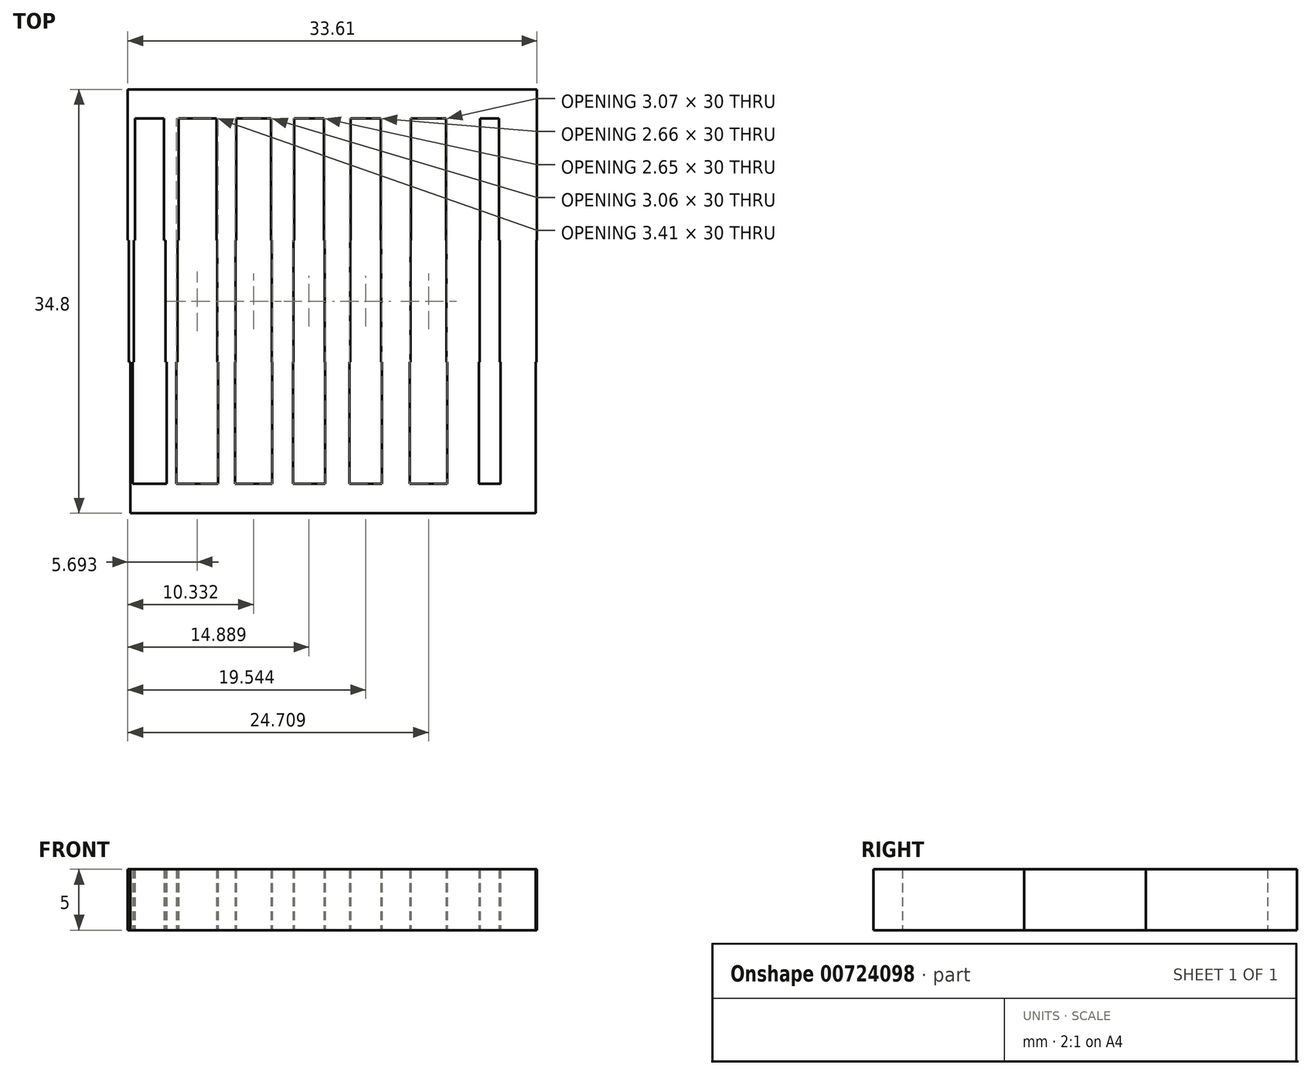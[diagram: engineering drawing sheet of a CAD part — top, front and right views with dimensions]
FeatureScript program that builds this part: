
annotation { "Feature Type Name" : "Feature", "Feature Type Description" : "" }
export const myFeature = defineFeature(function(context is Context, id is Id, definition is map)
    precondition{}
    {
        {
            var Q0;
            Q0=qCreatedBy(makeId("Top.planeOp"),FACE);
            var sketch = newSketch(context, id + "F0", { "sketchPlane" : qUnion([Q0])});
            skLineSegment(sketch, "E0.bottom", {"start": v(-34.1, -30) * mm, "end": v(-33.9, -30) * mm});
            skLineSegment(sketch, "E0.top", {"start": v(-34.1, -20) * mm, "end": v(-33.9, -20) * mm});
            skLineSegment(sketch, "E0.left", {"start": v(-34.1, -30) * mm, "end": v(-34.1, -20) * mm});
            skLineSegment(sketch, "E0.right", {"start": v(-33.9, -30) * mm, "end": v(-33.9, -20) * mm});
            skLineSegment(sketch, "E1.bottom", {"start": v(-34.2, -20) * mm, "end": v(-33.8, -20) * mm});
            skLineSegment(sketch, "E1.top", {"start": v(-34.2, -10) * mm, "end": v(-33.8, -10) * mm});
            skLineSegment(sketch, "E1.left", {"start": v(-34.2, -20) * mm, "end": v(-34.2, -10) * mm});
            skLineSegment(sketch, "E1.right", {"start": v(-33.8, -20) * mm, "end": v(-33.8, -10) * mm});
            skLineSegment(sketch, "E2.bottom", {"start": v(-34.3, -10) * mm, "end": v(-33.7, -10) * mm});
            skLineSegment(sketch, "E2.top", {"start": v(-34.3, 0) * mm, "end": v(-33.7, 0) * mm});
            skLineSegment(sketch, "E2.left", {"start": v(-34.3, -10) * mm, "end": v(-34.3, 0) * mm});
            skLineSegment(sketch, "E2.right", {"start": v(-33.7, -10) * mm, "end": v(-33.7, 0) * mm});
            skPoint(sketch, "E3", {"position": v(-34, -20) * mm});
            skPoint(sketch, "E4", {"position": v(-34, -10) * mm});
            skLineSegment(sketch, "E5.bottom", {"start": v(-31.11, -30) * mm, "end": v(-30.31, -30) * mm});
            skLineSegment(sketch, "E5.top", {"start": v(-31.11, -20) * mm, "end": v(-30.31, -20) * mm});
            skLineSegment(sketch, "E5.left", {"start": v(-31.11, -30) * mm, "end": v(-31.11, -20) * mm});
            skLineSegment(sketch, "E5.right", {"start": v(-30.31, -30) * mm, "end": v(-30.31, -20) * mm});
            skLineSegment(sketch, "E6.bottom", {"start": v(-31.21, -20) * mm, "end": v(-30.21, -20) * mm});
            skLineSegment(sketch, "E6.top", {"start": v(-31.21, -10) * mm, "end": v(-30.21, -10) * mm});
            skLineSegment(sketch, "E6.left", {"start": v(-31.21, -20) * mm, "end": v(-31.21, -10) * mm});
            skLineSegment(sketch, "E6.right", {"start": v(-30.21, -20) * mm, "end": v(-30.21, -10) * mm});
            skLineSegment(sketch, "E7.bottom", {"start": v(-31.31, -10) * mm, "end": v(-30.11, -10) * mm});
            skLineSegment(sketch, "E7.top", {"start": v(-31.31, 0) * mm, "end": v(-30.11, 0) * mm});
            skLineSegment(sketch, "E7.left", {"start": v(-31.31, -10) * mm, "end": v(-31.31, 0) * mm});
            skLineSegment(sketch, "E7.right", {"start": v(-30.11, -10) * mm, "end": v(-30.11, 0) * mm});
            skPoint(sketch, "E8", {"position": v(-30.71, -20) * mm});
            skPoint(sketch, "E9", {"position": v(-30.71, -10) * mm});
            skLineSegment(sketch, "E10.bottom", {"start": v(-22.44, -30) * mm, "end": v(-20.74, -30) * mm});
            skLineSegment(sketch, "E10.top", {"start": v(-22.44, -20) * mm, "end": v(-20.74, -20) * mm});
            skLineSegment(sketch, "E10.left", {"start": v(-22.44, -30) * mm, "end": v(-22.44, -20) * mm});
            skLineSegment(sketch, "E10.right", {"start": v(-20.74, -30) * mm, "end": v(-20.74, -20) * mm});
            skLineSegment(sketch, "E11.bottom", {"start": v(-22.49, -20) * mm, "end": v(-20.69, -20) * mm});
            skLineSegment(sketch, "E11.top", {"start": v(-22.49, -10) * mm, "end": v(-20.69, -10) * mm});
            skLineSegment(sketch, "E11.left", {"start": v(-22.49, -20) * mm, "end": v(-22.49, -10) * mm});
            skLineSegment(sketch, "E11.right", {"start": v(-20.69, -20) * mm, "end": v(-20.69, -10) * mm});
            skLineSegment(sketch, "E12.bottom", {"start": v(-22.54, -10) * mm, "end": v(-20.64, -10) * mm});
            skLineSegment(sketch, "E12.top", {"start": v(-22.54, 0) * mm, "end": v(-20.64, 0) * mm});
            skLineSegment(sketch, "E12.left", {"start": v(-22.54, -10) * mm, "end": v(-22.54, 0) * mm});
            skLineSegment(sketch, "E12.right", {"start": v(-20.64, -10) * mm, "end": v(-20.64, 0) * mm});
            skPoint(sketch, "E13", {"position": v(-21.59, -20) * mm});
            skPoint(sketch, "E14", {"position": v(-21.59, -10) * mm});
            skLineSegment(sketch, "E15.bottom", {"start": v(-18.08, -30) * mm, "end": v(-16.08, -30) * mm});
            skLineSegment(sketch, "E15.top", {"start": v(-18.08, -20) * mm, "end": v(-16.08, -20) * mm});
            skLineSegment(sketch, "E15.left", {"start": v(-18.08, -30) * mm, "end": v(-18.08, -20) * mm});
            skLineSegment(sketch, "E15.right", {"start": v(-16.08, -30) * mm, "end": v(-16.08, -20) * mm});
            skLineSegment(sketch, "E16.bottom", {"start": v(-18.13, -20) * mm, "end": v(-16.03, -20) * mm});
            skLineSegment(sketch, "E16.top", {"start": v(-18.13, -10) * mm, "end": v(-16.03, -10) * mm});
            skLineSegment(sketch, "E16.left", {"start": v(-18.13, -20) * mm, "end": v(-18.13, -10) * mm});
            skLineSegment(sketch, "E16.right", {"start": v(-16.03, -20) * mm, "end": v(-16.03, -10) * mm});
            skLineSegment(sketch, "E17.bottom", {"start": v(-18.18, -10) * mm, "end": v(-15.98, -10) * mm});
            skLineSegment(sketch, "E17.top", {"start": v(-18.18, 0) * mm, "end": v(-15.98, 0) * mm});
            skLineSegment(sketch, "E17.left", {"start": v(-18.18, -10) * mm, "end": v(-18.18, 0) * mm});
            skLineSegment(sketch, "E17.right", {"start": v(-15.98, -10) * mm, "end": v(-15.98, 0) * mm});
            skPoint(sketch, "E18", {"position": v(-17.08, -20) * mm});
            skPoint(sketch, "E19", {"position": v(-17.08, -10) * mm});
            skLineSegment(sketch, "E20.bottom", {"start": v(-13.43, -30) * mm, "end": v(-11.13, -30) * mm});
            skLineSegment(sketch, "E20.top", {"start": v(-13.43, -20) * mm, "end": v(-11.13, -20) * mm});
            skLineSegment(sketch, "E20.left", {"start": v(-13.43, -30) * mm, "end": v(-13.43, -20) * mm});
            skLineSegment(sketch, "E20.right", {"start": v(-11.13, -30) * mm, "end": v(-11.13, -20) * mm});
            skLineSegment(sketch, "E21.bottom", {"start": v(-13.48, -20) * mm, "end": v(-11.08, -20) * mm});
            skLineSegment(sketch, "E21.top", {"start": v(-13.48, -10) * mm, "end": v(-11.08, -10) * mm});
            skLineSegment(sketch, "E21.left", {"start": v(-13.48, -20) * mm, "end": v(-13.48, -10) * mm});
            skLineSegment(sketch, "E21.right", {"start": v(-11.08, -20) * mm, "end": v(-11.08, -10) * mm});
            skLineSegment(sketch, "E22.bottom", {"start": v(-13.53, -10) * mm, "end": v(-11.03, -10) * mm});
            skLineSegment(sketch, "E22.top", {"start": v(-13.53, 0) * mm, "end": v(-11.03, 0) * mm});
            skLineSegment(sketch, "E22.left", {"start": v(-13.53, -10) * mm, "end": v(-13.53, 0) * mm});
            skLineSegment(sketch, "E22.right", {"start": v(-11.03, -10) * mm, "end": v(-11.03, 0) * mm});
            skPoint(sketch, "E23", {"position": v(-12.28, -20) * mm});
            skPoint(sketch, "E24", {"position": v(-12.28, -10) * mm});
            skLineSegment(sketch, "E25.bottom", {"start": v(-8.05, -30) * mm, "end": v(-5.45, -30) * mm});
            skLineSegment(sketch, "E25.top", {"start": v(-8.05, -20) * mm, "end": v(-5.45, -20) * mm});
            skLineSegment(sketch, "E25.left", {"start": v(-8.05, -30) * mm, "end": v(-8.05, -20) * mm});
            skLineSegment(sketch, "E25.right", {"start": v(-5.45, -30) * mm, "end": v(-5.45, -20) * mm});
            skLineSegment(sketch, "E26.bottom", {"start": v(-8.1, -20) * mm, "end": v(-5.4, -20) * mm});
            skLineSegment(sketch, "E26.top", {"start": v(-8.1, -10) * mm, "end": v(-5.4, -10) * mm});
            skLineSegment(sketch, "E26.left", {"start": v(-8.1, -20) * mm, "end": v(-8.1, -10) * mm});
            skLineSegment(sketch, "E26.right", {"start": v(-5.4, -20) * mm, "end": v(-5.4, -10) * mm});
            skLineSegment(sketch, "E27.bottom", {"start": v(-8.15, -10) * mm, "end": v(-5.35, -10) * mm});
            skLineSegment(sketch, "E27.top", {"start": v(-8.15, 0) * mm, "end": v(-5.35, 0) * mm});
            skLineSegment(sketch, "E27.left", {"start": v(-8.15, -10) * mm, "end": v(-8.15, 0) * mm});
            skLineSegment(sketch, "E27.right", {"start": v(-5.35, -10) * mm, "end": v(-5.35, 0) * mm});
            skPoint(sketch, "E28", {"position": v(-6.75, -20) * mm});
            skPoint(sketch, "E29", {"position": v(-6.75, -10) * mm});
            skLineSegment(sketch, "E30.bottom", {"start": v(-3.69, -30) * mm, "end": v(-0.79, -30) * mm});
            skLineSegment(sketch, "E30.top", {"start": v(-3.69, -20) * mm, "end": v(-0.79, -20) * mm});
            skLineSegment(sketch, "E30.left", {"start": v(-3.69, -30) * mm, "end": v(-3.69, -20) * mm});
            skLineSegment(sketch, "E30.right", {"start": v(-0.79, -30) * mm, "end": v(-0.79, -20) * mm});
            skLineSegment(sketch, "E31.bottom", {"start": v(-3.74, -20) * mm, "end": v(-0.74, -20) * mm});
            skLineSegment(sketch, "E31.top", {"start": v(-3.74, -10) * mm, "end": v(-0.74, -10) * mm});
            skLineSegment(sketch, "E31.left", {"start": v(-3.74, -20) * mm, "end": v(-3.74, -10) * mm});
            skLineSegment(sketch, "E31.right", {"start": v(-0.74, -20) * mm, "end": v(-0.74, -10) * mm});
            skLineSegment(sketch, "E32.bottom", {"start": v(-3.79, -10) * mm, "end": v(-0.69, -10) * mm});
            skLineSegment(sketch, "E32.top", {"start": v(-3.79, 0) * mm, "end": v(-0.69, 0) * mm});
            skLineSegment(sketch, "E32.left", {"start": v(-3.79, -10) * mm, "end": v(-3.79, 0) * mm});
            skLineSegment(sketch, "E32.right", {"start": v(-0.69, -10) * mm, "end": v(-0.69, 0) * mm});
            skPoint(sketch, "E33", {"position": v(-2.24, -20) * mm});
            skPoint(sketch, "E34", {"position": v(-2.24, -10) * mm});
            skLineSegment(sketch, "E35.bottom", {"start": v(-26.9, -30) * mm, "end": v(-25.5, -30) * mm});
            skLineSegment(sketch, "E35.top", {"start": v(-26.9, -20) * mm, "end": v(-25.5, -20) * mm});
            skLineSegment(sketch, "E35.left", {"start": v(-26.9, -30) * mm, "end": v(-26.9, -20) * mm});
            skLineSegment(sketch, "E35.right", {"start": v(-25.5, -30) * mm, "end": v(-25.5, -20) * mm});
            skLineSegment(sketch, "E36.bottom", {"start": v(-26.95, -20) * mm, "end": v(-25.45, -20) * mm});
            skLineSegment(sketch, "E36.top", {"start": v(-26.95, -10) * mm, "end": v(-25.45, -10) * mm});
            skLineSegment(sketch, "E36.left", {"start": v(-26.95, -20) * mm, "end": v(-26.95, -10) * mm});
            skLineSegment(sketch, "E36.right", {"start": v(-25.45, -20) * mm, "end": v(-25.45, -10) * mm});
            skLineSegment(sketch, "E37.bottom", {"start": v(-27, -10) * mm, "end": v(-25.4, -10) * mm});
            skLineSegment(sketch, "E37.top", {"start": v(-27, 0) * mm, "end": v(-25.4, 0) * mm});
            skLineSegment(sketch, "E37.left", {"start": v(-27, -10) * mm, "end": v(-27, 0) * mm});
            skLineSegment(sketch, "E37.right", {"start": v(-25.4, -10) * mm, "end": v(-25.4, 0) * mm});
            skPoint(sketch, "E38", {"position": v(-26.2, -20) * mm});
            skPoint(sketch, "E39", {"position": v(-26.2, -10) * mm});
            skLineSegment(sketch, "E40.bottom", {"start": v(-34.3, 0) * mm, "end": v(-0.69, 0) * mm});
            skLineSegment(sketch, "E40.top", {"start": v(-34.3, 2.4) * mm, "end": v(-0.69, 2.4) * mm});
            skLineSegment(sketch, "E40.left", {"start": v(-34.3, 0) * mm, "end": v(-34.3, 2.4) * mm});
            skLineSegment(sketch, "E40.right", {"start": v(-0.69, 0) * mm, "end": v(-0.69, 2.4) * mm});
            skLineSegment(sketch, "E41.bottom", {"start": v(-0.79, -30) * mm, "end": v(-34.1, -30) * mm});
            skLineSegment(sketch, "E41.top", {"start": v(-0.79, -32.4) * mm, "end": v(-34.1, -32.4) * mm});
            skLineSegment(sketch, "E41.left", {"start": v(-0.79, -30) * mm, "end": v(-0.79, -32.4) * mm});
            skLineSegment(sketch, "E41.right", {"start": v(-34.1, -30) * mm, "end": v(-34.1, -32.4) * mm});
            skSolve(sketch);
        }
        {
            var Q0;
            Q0 = qSketchRegion(id + "F0", true);
            var Q1;
            {var subQ0=sQuery(id+"F0.wireOp",EDGE,"E7.left");Q1=makeQuery(id+"F0.imprint","IMPRINT",FACE,{"disambiguationData":[TD([[makeQuery(id+"F0.imprint","IMPRINT",EDGE,{"derivedFrom":subQ0}),-1.0]])]});}
            var Q2;
            {var subQ0=sQuery(id+"F0.wireOp",EDGE,"E37.left");Q2=makeQuery(id+"F0.imprint","IMPRINT",FACE,{"disambiguationData":[TD([[makeQuery(id+"F0.imprint","IMPRINT",EDGE,{"derivedFrom":subQ0}),-1.0]])]});}
            var Q3;
            {var subQ0=sQuery(id+"F0.wireOp",EDGE,"E12.left");Q3=makeQuery(id+"F0.imprint","IMPRINT",FACE,{"disambiguationData":[TD([[makeQuery(id+"F0.imprint","IMPRINT",EDGE,{"derivedFrom":subQ0}),-1.0]])]});}
            var Q4;
            {var subQ0=sQuery(id+"F0.wireOp",EDGE,"E17.left");Q4=makeQuery(id+"F0.imprint","IMPRINT",FACE,{"disambiguationData":[TD([[makeQuery(id+"F0.imprint","IMPRINT",EDGE,{"derivedFrom":subQ0}),-1.0]])]});}
            var Q5;
            {var subQ0=sQuery(id+"F0.wireOp",EDGE,"E22.left");Q5=makeQuery(id+"F0.imprint","IMPRINT",FACE,{"disambiguationData":[TD([[makeQuery(id+"F0.imprint","IMPRINT",EDGE,{"derivedFrom":subQ0}),-1.0]])]});}
            var Q6;
            {var subQ0=sQuery(id+"F0.wireOp",EDGE,"E27.left");Q6=makeQuery(id+"F0.imprint","IMPRINT",FACE,{"disambiguationData":[TD([[makeQuery(id+"F0.imprint","IMPRINT",EDGE,{"derivedFrom":subQ0}),-1.0]])]});}
            var Q7;
            {var subQ0=sQuery(id+"F0.wireOp",EDGE,"E25.left");Q7=makeQuery(id+"F0.imprint","IMPRINT",FACE,{"disambiguationData":[TD([[makeQuery(id+"F0.imprint","IMPRINT",EDGE,{"derivedFrom":subQ0}),-1.0]])]});}
            var Q8;
            {var subQ0=sQuery(id+"F0.wireOp",EDGE,"E20.left");Q8=makeQuery(id+"F0.imprint","IMPRINT",FACE,{"disambiguationData":[TD([[makeQuery(id+"F0.imprint","IMPRINT",EDGE,{"derivedFrom":subQ0}),-1.0]])]});}
            var Q9;
            {var subQ0=sQuery(id+"F0.wireOp",EDGE,"E21.left");Q9=makeQuery(id+"F0.imprint","IMPRINT",FACE,{"disambiguationData":[TD([[makeQuery(id+"F0.imprint","IMPRINT",EDGE,{"derivedFrom":subQ0}),-1.0]])]});}
            var Q10;
            {var subQ0=sQuery(id+"F0.wireOp",EDGE,"E16.left");Q10=makeQuery(id+"F0.imprint","IMPRINT",FACE,{"disambiguationData":[TD([[makeQuery(id+"F0.imprint","IMPRINT",EDGE,{"derivedFrom":subQ0}),-1.0]])]});}
            var Q11;
            {var subQ0=sQuery(id+"F0.wireOp",EDGE,"E15.left");Q11=makeQuery(id+"F0.imprint","IMPRINT",FACE,{"disambiguationData":[TD([[makeQuery(id+"F0.imprint","IMPRINT",EDGE,{"derivedFrom":subQ0}),-1.0]])]});}
            var Q12;
            {var subQ0=sQuery(id+"F0.wireOp",EDGE,"E10.left");Q12=makeQuery(id+"F0.imprint","IMPRINT",FACE,{"disambiguationData":[TD([[makeQuery(id+"F0.imprint","IMPRINT",EDGE,{"derivedFrom":subQ0}),-1.0]])]});}
            var Q13;
            {var subQ0=sQuery(id+"F0.wireOp",EDGE,"E11.left");Q13=makeQuery(id+"F0.imprint","IMPRINT",FACE,{"disambiguationData":[TD([[makeQuery(id+"F0.imprint","IMPRINT",EDGE,{"derivedFrom":subQ0}),-1.0]])]});}
            var Q14;
            {var subQ0=sQuery(id+"F0.wireOp",EDGE,"E36.left");Q14=makeQuery(id+"F0.imprint","IMPRINT",FACE,{"disambiguationData":[TD([[makeQuery(id+"F0.imprint","IMPRINT",EDGE,{"derivedFrom":subQ0}),-1.0]])]});}
            var Q15;
            {var subQ0=sQuery(id+"F0.wireOp",EDGE,"E35.left");Q15=makeQuery(id+"F0.imprint","IMPRINT",FACE,{"disambiguationData":[TD([[makeQuery(id+"F0.imprint","IMPRINT",EDGE,{"derivedFrom":subQ0}),-1.0]])]});}
            var Q16;
            {var subQ0=sQuery(id+"F0.wireOp",EDGE,"E6.left");Q16=makeQuery(id+"F0.imprint","IMPRINT",FACE,{"disambiguationData":[TD([[makeQuery(id+"F0.imprint","IMPRINT",EDGE,{"derivedFrom":subQ0}),-1.0]])]});}
            var Q17;
            {var subQ0=sQuery(id+"F0.wireOp",EDGE,"E5.left");Q17=makeQuery(id+"F0.imprint","IMPRINT",FACE,{"disambiguationData":[TD([[makeQuery(id+"F0.imprint","IMPRINT",EDGE,{"derivedFrom":subQ0}),-1.0]])]});}
            var Q18;
            {var subQ0=sQuery(id+"F0.wireOp",EDGE,"E26.left");Q18=makeQuery(id+"F0.imprint","IMPRINT",FACE,{"disambiguationData":[TD([[makeQuery(id+"F0.imprint","IMPRINT",EDGE,{"derivedFrom":subQ0}),-1.0]])]});}
            extrude(context, id + "F1", {"entities" : qUnion([Q0, Q1, Q2, Q3, Q4, Q5, Q6, Q7, Q8, Q9, Q10, Q11, Q12, Q13, Q14, Q15, Q16, Q17, Q18]), "depth" : 5 * mm, "offsetDistance" : 25 * mm});
        }
    });
